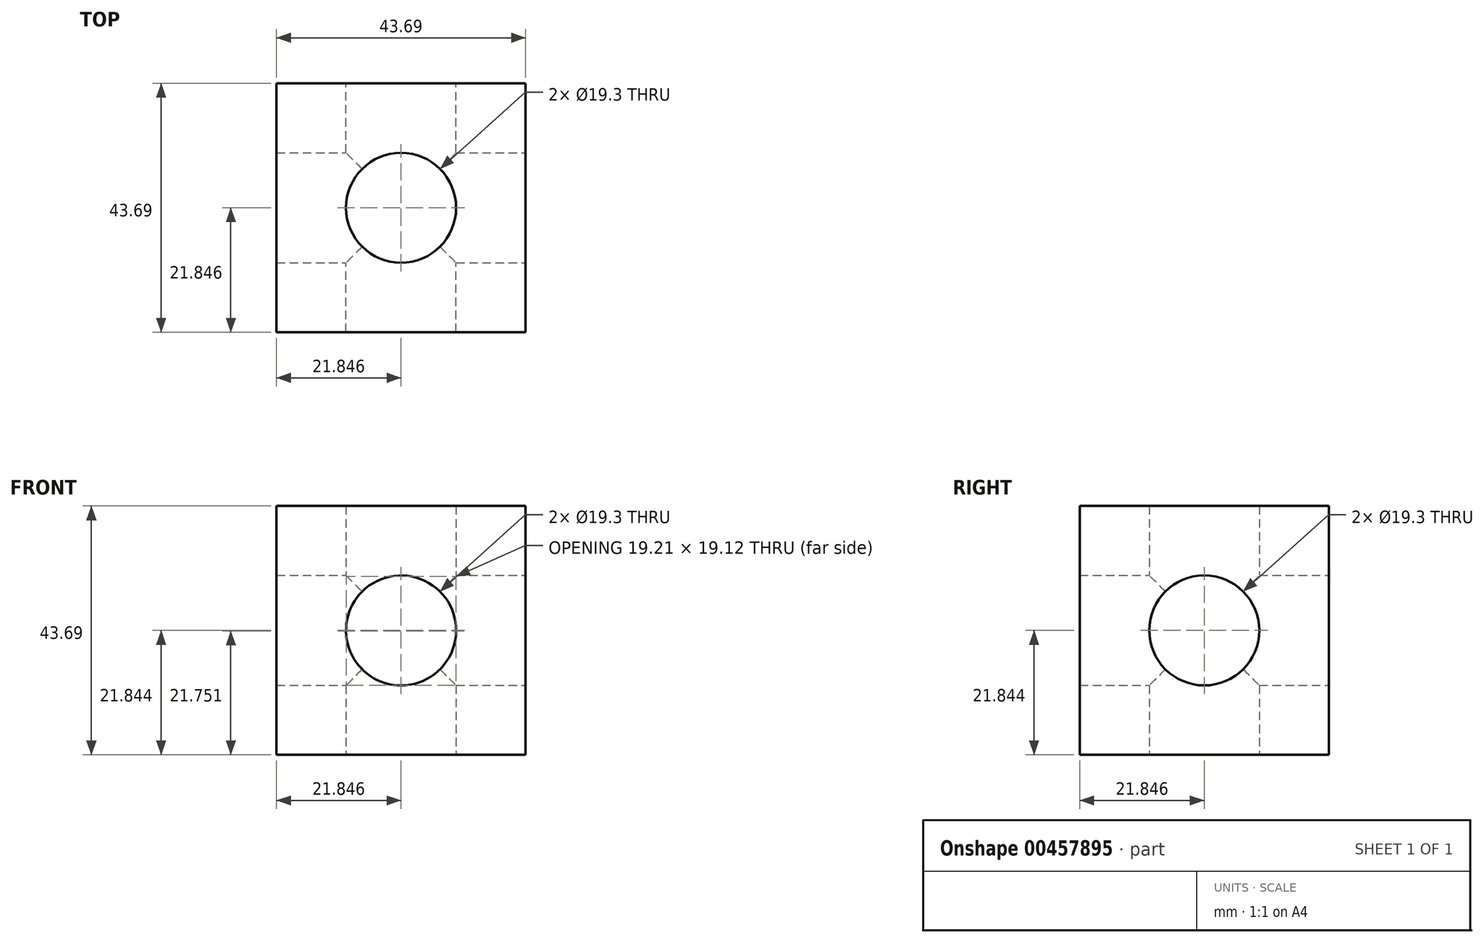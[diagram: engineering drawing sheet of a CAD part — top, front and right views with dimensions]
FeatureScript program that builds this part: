
annotation { "Feature Type Name" : "Feature", "Feature Type Description" : "" }
export const myFeature = defineFeature(function(context is Context, id is Id, definition is map)
    precondition{}
    {
        {
            var Q0;
            Q0=qCreatedBy(makeId("Front.planeOp"),FACE);
            var sketch = newSketch(context, id + "F0", { "sketchPlane" : qUnion([Q0])});
            skLineSegment(sketch, "E0.bottom", {"start": v(0, 0) * mm, "end": v(-43.69, 0) * mm});
            skLineSegment(sketch, "E0.top", {"start": v(0, 43.69) * mm, "end": v(-43.69, 43.69) * mm});
            skLineSegment(sketch, "E0.left", {"start": v(0, 0) * mm, "end": v(0, 43.69) * mm});
            skLineSegment(sketch, "E0.right", {"start": v(-43.69, 0) * mm, "end": v(-43.69, 43.69) * mm});
            skCircle(sketch, "E1", {"center": v(-21.84, 21.84) * mm, "radius": 9.65 * mm});
            skLineSegment(sketch, "E2", {"start": v(-43.69, 43.69) * mm, "end": v(0, 43.69) * mm});
            skSolve(sketch);
        }
        {
            var Q0;
            Q0=makeQuery(id+"F0.imprint","IMPRINT",FACE,{"disambiguationData":[TD([[makeQuery(id+"F0.imprint","IMPRINT",EDGE,{"derivedFrom":sQuery(id+"F0.wireOp",EDGE,"E0.bottom")}),-1.0]])]});
            extrude(context, id + "F1", {"entities" : qUnion([Q0]), "depth" : 43.69 * mm});
        }
        {
            var Q0;
            Q0=makeQuery(id+"F1.opExtrude","SWEPT_FACE",FACE,{"disambiguationData":[OSD([sQuery(id+"F0.wireOp",EDGE,"E0.bottom")])]});
            var sketch = newSketch(context, id + "F2", { "sketchPlane" : qUnion([Q0])});
            skLineSegment(sketch, "E3", {"start": v(-21.84, 43.69) * mm, "end": v(-21.84, 0) * mm, "construction": true});
            skLineSegment(sketch, "E4", {"start": v(-43.69, 21.84) * mm, "end": v(0, 21.84) * mm, "construction": true});
            skCircle(sketch, "E5", {"center": v(-21.84, 21.84) * mm, "radius": 9.65 * mm});
            skSolve(sketch);
        }
        {
            var Q0;
            Q0=makeQuery(id+"F2.imprint","IMPRINT",FACE,{"disambiguationData":[TD([[makeQuery(id+"F2.imprint","IMPRINT",EDGE,{"derivedFrom":sQuery(id+"F2.wireOp",EDGE,"E5")}),1.0]])]});
            var Q1;
            Q1=sQuery(id+"F2.wireOp",EDGE,"E5");
            extrude(context, id + "F3", {"entities" : qUnion([Q0]), "operationType" : NewBodyOperationType.REMOVE, "surfaceEntities" : qUnion([Q1]), "endBound" : BoundingType.THROUGH_ALL, "oppositeDirection" : true, "depth" : 25.4 * mm, "offsetDistance" : 25.4 * mm});
        }
        {
            var Q0;
            Q0=qCreatedBy(makeId("Right.planeOp"),FACE);
            var sketch = newSketch(context, id + "F4", { "sketchPlane" : qUnion([Q0])});
            skLineSegment(sketch, "E6", {"start": v(0, 43.69) * mm, "end": v(0, 0) * mm, "construction": true});
            skLineSegment(sketch, "E7", {"start": v(0, 0) * mm, "end": v(-43.69, 0) * mm, "construction": true});
            skLineSegment(sketch, "E8", {"start": v(-43.69, 0) * mm, "end": v(-43.69, 43.69) * mm, "construction": true});
            skLineSegment(sketch, "E9", {"start": v(-43.69, 43.69) * mm, "end": v(0, 43.69) * mm, "construction": true});
            skCircle(sketch, "E10", {"center": v(-21.84, 21.84) * mm, "radius": 9.65 * mm});
            skSolve(sketch);
        }
        {
            var Q0;
            Q0=makeQuery(id+"F4.imprint","IMPRINT",FACE,{"disambiguationData":[TD([[makeQuery(id+"F4.imprint","IMPRINT",EDGE,{"derivedFrom":sQuery(id+"F4.wireOp",EDGE,"E10")}),1.0]])]});
            extrude(context, id + "F5", {"entities" : qUnion([Q0]), "operationType" : NewBodyOperationType.REMOVE, "endBound" : BoundingType.THROUGH_ALL, "oppositeDirection" : true, "depth" : 25.4 * mm, "offsetDistance" : 25.4 * mm});
        }
    });
